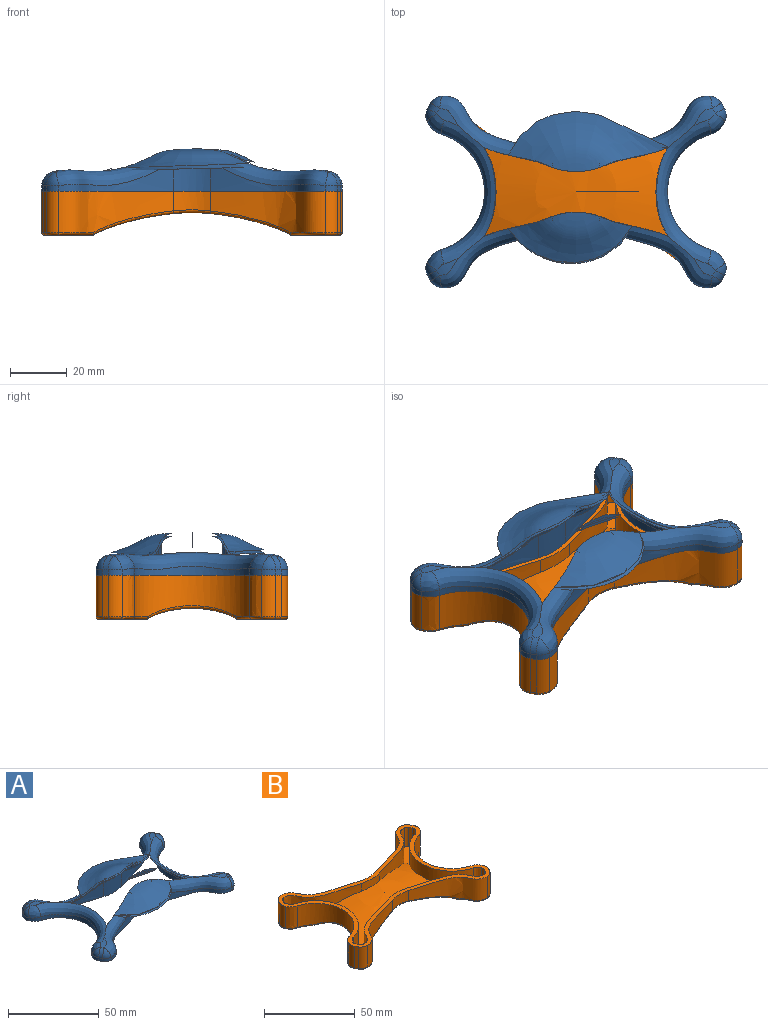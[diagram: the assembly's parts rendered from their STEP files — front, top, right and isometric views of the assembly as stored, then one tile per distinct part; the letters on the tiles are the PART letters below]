
ASSEMBLY  parts=2 mates=1
PART A: 107 faces, bbox 106.7x73.2x17.5 mm
  f0: plane 106.75x70.16mm, normal (0,0,-1), area 398.4mm2, adj f5,f6,f7,f10,f11,f13,f14,f15
  f1: revolved ~72.28x72.28mm, area 1741.4mm2, adj f35,f42,f43,f47,f48,f49,f50,f51
  f2: revolved ~9.21x7.37mm, area 20mm2, adj f12,f37,f43,f48
  f3: revolved ~9.21x7.37mm, area 20mm2, adj f20,f35,f36,f43
  f4: revolved ~9.21x7.37mm, area 20mm2, adj f8,f45,f49,f51
  f5: extruded ~4.79x4.26mm, area 14.9mm2, adj f0,f22,f32,f45
  f6: extruded ~4.79x4.26mm, area 14.9mm2, adj f0,f23,f28,f37
  f7: cylinder r=60mm len=2mm, axis (0,0,-1), area 4.4mm2, adj f0,f8,f32,f53
  f8: torus R=55mm, axis (0,0,-1), area 14.2mm2, adj f4,f7,f39,f52
  f9: revolved ~9.21x7.37mm, area 20mm2, adj f17,f46,f47,f49
  f10: extruded ~40.46x20.84mm, area 177.5mm2, adj f0,f25,f51,f53
  f11: cylinder r=60mm len=2mm, axis (0,0,-1), area 4.4mm2, adj f0,f12,f28,f38
  f12: torus R=55mm, axis (0,0,-1), area 14.2mm2, adj f2,f11,f31,f44
  f13: extruded ~40.46x20.84mm, area 177.5mm2, adj f0,f25,f38,f48
  f14: extruded ~4.79x4.26mm, area 14.9mm2, adj f0,f22,f33,f46
  f15: extruded ~4.79x4.26mm, area 14.9mm2, adj f0,f23,f27,f36
  f16: cylinder r=60mm len=2mm, axis (0,0,-1), area 4.4mm2, adj f0,f17,f33,f34
  f17: torus R=55mm, axis (0,0,-1), area 14.2mm2, adj f9,f16,f40,f41
  f18: extruded ~40.46x20.84mm, area 177.5mm2, adj f0,f24,f34,f47
  f19: cylinder r=60mm len=2mm, axis (0,0,-1), area 4.4mm2, adj f0,f20,f26,f27
  f20: torus R=55mm, axis (0,0,-1), area 14.2mm2, adj f3,f19,f29,f30
  f21: extruded ~40.46x20.84mm, area 177.5mm2, adj f0,f24,f26,f35
  f22: cylinder r=21.18mm len=40.7mm, axis (0,0,-1), area 131.2mm2, adj f0,f5,f14,f49
  f23: cylinder r=21.18mm len=40.7mm, axis (0,0,-1), area 131.2mm2, adj f0,f6,f15,f43
  f24: cylinder r=21.18mm len=12.96mm, axis (0,0,-1), area 123.5mm2, adj f0,f18,f21,f42
  f25: cylinder r=21.18mm len=12.96mm, axis (0,0,-1), area 123.5mm2, adj f0,f10,f13,f50
  f26: cylinder r=5mm len=4.22mm, axis (0,0,-1), area 10.1mm2, adj f0,f19,f21,f29
  f27: cylinder r=5mm len=4.85mm, axis (0,0,-1), area 10.1mm2, adj f0,f15,f19,f30
  f28: cylinder r=5mm len=4.85mm, axis (0,0,-1), area 10.1mm2, adj f0,f6,f11,f31
  f29: sphere r=5mm, area 22.3mm2, adj f20,f26,f35
  f30: sphere r=5mm, area 22.4mm2, adj f20,f27,f36
  f31: sphere r=5mm, area 22.4mm2, adj f12,f28,f37
  f32: cylinder r=5mm len=4.85mm, axis (0,0,-1), area 10.1mm2, adj f0,f5,f7,f39
  f33: cylinder r=5mm len=4.85mm, axis (0,0,-1), area 10.1mm2, adj f0,f14,f16,f40
  f34: cylinder r=5mm len=4.22mm, axis (0,0,-1), area 10.1mm2, adj f0,f16,f18,f41
  f35: bspline ~43.55x25.83mm, area 367.1mm2, adj f1,f3,f21,f29,f42,f43
  f36: bspline ~7.62x6.92mm, area 42.9mm2, adj f3,f15,f30,f43
  f37: bspline ~7.52x6.6mm, area 42.9mm2, adj f2,f6,f31,f43
  f38: cylinder r=5mm len=4.22mm, axis (0,0,-1), area 10.1mm2, adj f0,f11,f13,f44
  f39: sphere r=5mm, area 22.4mm2, adj f8,f32,f45
  f40: sphere r=5mm, area 22.4mm2, adj f17,f33,f46
  f41: sphere r=5mm, area 20.1mm2, adj f17,f34,f47
  f42: bspline ~18.18x6.2mm, area 114.7mm2, adj f1,f24,f35,f47
  f43: bspline ~51.29x20.77mm, area 447.9mm2, adj f1,f2,f3,f23,f35,f36,f37,f48
  f44: sphere r=5mm, area 20.1mm2, adj f12,f38,f48
  f45: bspline ~7.62x6.92mm, area 42.9mm2, adj f4,f5,f39,f49
  f46: bspline ~7.52x6.6mm, area 42.9mm2, adj f9,f14,f40,f49
  f47: bspline ~42.5x25.43mm, area 367.1mm2, adj f1,f9,f18,f41,f42,f49
  f48: bspline ~42.5x25.43mm, area 367.1mm2, adj f1,f2,f13,f43,f44,f50
  f49: bspline ~51.29x20.77mm, area 447.9mm2, adj f1,f4,f9,f22,f45,f46,f47,f51
  f50: bspline ~18.18x6.2mm, area 114.7mm2, adj f1,f25,f48,f51
  f51: bspline ~43.55x25.83mm, area 367.1mm2, adj f1,f4,f10,f49,f50,f52
  f52: sphere r=5mm, area 22.3mm2, adj f8,f51,f53
  f53: cylinder r=5mm len=4.22mm, axis (0,0,-1), area 10.1mm2, adj f0,f7,f10,f52
  f54: revolved ~72.22x72.22mm, area 1719.6mm2, adj f88,f95,f96,f100,f101,f102,f103,f104
  f55: revolved ~8.96x7.22mm, area 19.2mm2, adj f65,f90,f96,f101
  f56: revolved ~8.96x7.22mm, area 19.2mm2, adj f73,f88,f89,f96
  f57: revolved ~8.96x7.22mm, area 19.2mm2, adj f61,f98,f102,f104
  f58: extruded ~4.19x3.78mm, area 13.1mm2, adj f0,f75,f85,f98
  f59: extruded ~4.19x3.78mm, area 13.1mm2, adj f0,f76,f81,f90
  f60: cylinder r=59mm len=2mm, axis (0,0,-1), area 4.3mm2, adj f0,f61,f85,f106
  f61: torus R=55mm, axis (0,0,-1), area 11.2mm2, adj f57,f60,f92,f105
  f62: revolved ~8.96x7.22mm, area 19.2mm2, adj f70,f99,f100,f102
  f63: extruded ~40.14x20.79mm, area 176.4mm2, adj f0,f78,f104,f106
  f64: cylinder r=59mm len=2mm, axis (0,0,-1), area 4.3mm2, adj f0,f65,f81,f91
  f65: torus R=55mm, axis (0,0,-1), area 11.2mm2, adj f55,f64,f84,f97
  f66: extruded ~40.14x20.79mm, area 176.4mm2, adj f0,f78,f91,f101
  f67: extruded ~4.19x3.78mm, area 13.1mm2, adj f0,f75,f86,f99
  f68: extruded ~4.19x3.78mm, area 13.1mm2, adj f0,f76,f80,f89
  f69: cylinder r=59mm len=2mm, axis (0,0,-1), area 4.3mm2, adj f0,f70,f86,f87
  f70: torus R=55mm, axis (0,0,-1), area 11.2mm2, adj f62,f69,f93,f94
  f71: extruded ~40.14x20.79mm, area 176.4mm2, adj f0,f77,f87,f100
  f72: cylinder r=59mm len=2mm, axis (0,0,-1), area 4.3mm2, adj f0,f73,f79,f80
  f73: torus R=55mm, axis (0,0,-1), area 11.2mm2, adj f56,f72,f82,f83
  f74: extruded ~40.14x20.79mm, area 176.4mm2, adj f0,f77,f79,f88
  f75: cylinder r=22.18mm len=42.62mm, axis (0,0,-1), area 137.4mm2, adj f0,f58,f67,f102
  f76: cylinder r=22.18mm len=42.62mm, axis (0,0,-1), area 137.4mm2, adj f0,f59,f68,f96
  f77: cylinder r=22.18mm len=13.57mm, axis (0,0,-1), area 129.3mm2, adj f0,f71,f74,f95
  f78: cylinder r=22.18mm len=13.57mm, axis (0,0,-1), area 129.3mm2, adj f0,f63,f66,f103
  f79: cylinder r=4mm len=3.37mm, axis (0,0,-1), area 8.1mm2, adj f0,f72,f74,f82
  f80: cylinder r=4mm len=3.88mm, axis (0,0,-1), area 8.1mm2, adj f0,f68,f72,f83
  f81: cylinder r=4mm len=3.88mm, axis (0,0,-1), area 8.1mm2, adj f0,f59,f64,f84
  f82: sphere r=4mm, area 14.2mm2, adj f73,f79,f88
  f83: sphere r=4mm, area 14.3mm2, adj f73,f80,f89
  f84: sphere r=4mm, area 12.9mm2, adj f65,f81,f90
  f85: cylinder r=4mm len=3.88mm, axis (0,0,-1), area 8.1mm2, adj f0,f58,f60,f92
  f86: cylinder r=4mm len=3.88mm, axis (0,0,-1), area 8.1mm2, adj f0,f67,f69,f93
  f87: cylinder r=4mm len=3.37mm, axis (0,0,-1), area 8.1mm2, adj f0,f69,f71,f94
  f88: bspline ~43.02x24.9mm, area 292.3mm2, adj f54,f56,f74,f82,f95,f96
  f89: bspline ~6.19x4.98mm, area 30.7mm2, adj f56,f68,f83,f96
  f90: bspline ~6.19x4.98mm, area 30.7mm2, adj f55,f59,f84,f96
  f91: cylinder r=4mm len=3.37mm, axis (0,0,-1), area 8.1mm2, adj f0,f64,f66,f97
  f92: sphere r=4mm, area 14.3mm2, adj f61,f85,f98
  f93: sphere r=4mm, area 12.9mm2, adj f70,f86,f99
  f94: sphere r=4mm, area 14.2mm2, adj f70,f87,f100
  f95: bspline ~16.98x4.84mm, area 93.1mm2, adj f54,f77,f88,f100
  f96: bspline ~50.65x19.13mm, area 368mm2, adj f54,f55,f56,f76,f88,f89,f90,f101
  f97: sphere r=4mm, area 14.2mm2, adj f65,f91,f101
  f98: bspline ~6.19x4.98mm, area 30.7mm2, adj f57,f58,f92,f102
  f99: bspline ~6.19x4.98mm, area 30.7mm2, adj f62,f67,f93,f102
  f100: bspline ~42.05x24.52mm, area 292.3mm2, adj f54,f62,f71,f94,f95,f102
  f101: bspline ~42.05x24.52mm, area 292.3mm2, adj f54,f55,f66,f96,f97,f103
  f102: bspline ~50.65x19.13mm, area 368mm2, adj f54,f57,f62,f75,f98,f99,f100,f104
  f103: bspline ~16.98x4.84mm, area 93.1mm2, adj f54,f78,f101,f104
  f104: bspline ~43.02x24.9mm, area 292.3mm2, adj f54,f57,f63,f102,f103,f105
  f105: sphere r=4mm, area 14.2mm2, adj f61,f104,f106
  f106: cylinder r=4mm len=3.37mm, axis (0,0,-1), area 8.1mm2, adj f0,f60,f63,f105
PART B: 103 faces, bbox 119.4x84.8x17.4 mm
  f0: extruded ~40.46x20.84mm, area 548.2mm2, adj f1,f12,f28,f41,f42
  f1: cylinder r=21.18mm len=12.96mm, axis (0,0,1), area 90.8mm2, adj f0,f2,f28,f37
  f2: extruded ~40.46x20.84mm, area 548.2mm2, adj f1,f13,f28,f32,f33
  f3: cylinder r=21.18mm len=40.7mm, axis (0,0,1), area 705mm2, adj f16,f17,f28,f44,f52,f53
  f4: extruded ~40.46x20.84mm, area 548.2mm2, adj f5,f20,f28,f64,f70
  f5: cylinder r=21.18mm len=12.96mm, axis (0,0,1), area 90.8mm2, adj f4,f6,f28,f72
  f6: extruded ~40.46x20.84mm, area 548.2mm2, adj f5,f21,f28,f68,f73
  f7: cylinder r=21.18mm len=40.7mm, axis (0,0,1), area 705mm2, adj f24,f25,f28,f50,f61,f62
  f8: plane 16.64x16.49mm, normal (0,0,-1), area 155.2mm2, adj f30,f31,f33,f34,f39,f43,f44
  f9: plane 16.64x16.49mm, normal (0,0,-1), area 155.2mm2, adj f35,f36,f40,f41,f45,f50,f51
  f10: plane 16.64x16.49mm, normal (0,0,-1), area 155.2mm2, adj f55,f56,f60,f61,f65,f68,f69
  f11: cylinder r=60mm len=14.5mm, axis (0,0,1), area 32mm2, adj f12,f26,f28,f35
  f12: cylinder r=5mm len=14.5mm, axis (0,0,1), area 73.4mm2, adj f0,f11,f28,f36
  f13: cylinder r=5mm len=14.5mm, axis (0,0,1), area 73.4mm2, adj f2,f14,f28,f30
  f14: cylinder r=60mm len=14.5mm, axis (0,0,1), area 32mm2, adj f13,f15,f28,f31
  f15: cylinder r=5mm len=14.5mm, axis (0,0,1), area 73.4mm2, adj f14,f16,f28,f34
  f16: extruded ~14.5x4.79mm, area 95.6mm2, adj f3,f15,f28,f39
  f17: extruded ~14.5x4.79mm, area 95.6mm2, adj f3,f18,f28,f48
  f18: cylinder r=5mm len=14.5mm, axis (0,0,1), area 73.4mm2, adj f17,f19,f28,f49
  f19: cylinder r=60mm len=14.5mm, axis (0,0,1), area 32mm2, adj f18,f20,f28,f54
  f20: cylinder r=5mm len=14.5mm, axis (0,0,1), area 73.4mm2, adj f4,f19,f28,f59
  f21: cylinder r=5mm len=14.5mm, axis (0,0,1), area 73.4mm2, adj f6,f22,f28,f65
  f22: cylinder r=60mm len=14.5mm, axis (0,0,1), area 32mm2, adj f21,f23,f28,f60
  f23: cylinder r=5mm len=14.5mm, axis (0,0,1), area 73.4mm2, adj f22,f24,f28,f55
  f24: extruded ~14.5x4.79mm, area 95.6mm2, adj f7,f23,f28,f56
  f25: extruded ~14.5x4.79mm, area 95.6mm2, adj f7,f26,f28,f45
  f26: cylinder r=5mm len=14.5mm, axis (0,0,1), area 73.4mm2, adj f11,f25,f28,f40
  f27: plane 16.64x16.49mm, normal (0,0,-1), area 155.2mm2, adj f48,f49,f53,f54,f59,f63,f64
  f28: plane 106.85x68.65mm, normal (0,0,1), area 983.5mm2, adj f0,f1,f2,f3,f4,f5,f6,f7
  f29: sphere r=105mm, area 2088.8mm2, adj f32,f37,f42,f43,f51,f52,f62,f63
  f30: torus R=4mm, axis (0,0,1), area 7.4mm2, adj f8,f13,f31,f33
  f31: torus R=59mm, axis (0,0,1), area 3.4mm2, adj f8,f14,f30,f34
  f32: bspline ~38.56x14.8mm, area 51mm2, adj f2,f29,f37,f38
  f33: bspline ~25.9x12.77mm, area 27.1mm2, adj f2,f8,f30,f38
  f34: torus R=4mm, axis (0,0,1), area 7.4mm2, adj f8,f15,f31,f39
  f35: torus R=59mm, axis (0,0,1), area 3.4mm2, adj f9,f11,f36,f40
  f36: torus R=4mm, axis (0,0,1), area 7.4mm2, adj f9,f12,f35,f41
  f37: bspline ~18.02x2.96mm, area 22.2mm2, adj f1,f29,f32,f42
  f38: sphere r=1mm, area 0.4mm2, adj f32,f33,f43
  f39: bspline ~7.07x6.87mm, area 9.9mm2, adj f8,f16,f34,f44
  f40: torus R=4mm, axis (0,0,1), area 7.4mm2, adj f9,f26,f35,f45
  f41: bspline ~25.9x12.77mm, area 27.1mm2, adj f0,f9,f36,f46
  f42: bspline ~40.35x14.93mm, area 51mm2, adj f0,f29,f37,f46
  f43: torus R=41.6mm, axis (0,0,1), area 2.6mm2, adj f8,f29,f38,f47
  f44: torus R=22.18mm, axis (0,0,1), area 15.8mm2, adj f3,f8,f39,f47
  f45: bspline ~7.07x6.87mm, area 9.9mm2, adj f9,f25,f40,f50
  f46: sphere r=1mm, area 0.4mm2, adj f41,f42,f51
  f47: sphere r=1mm, area 0.4mm2, adj f43,f44,f52
  f48: bspline ~7.07x6.87mm, area 9.9mm2, adj f17,f27,f49,f53
  f49: torus R=4mm, axis (0,0,1), area 7.4mm2, adj f18,f27,f48,f54
  f50: torus R=22.18mm, axis (0,0,1), area 15.8mm2, adj f7,f9,f45,f57
  f51: torus R=41.6mm, axis (0,0,1), area 2.6mm2, adj f9,f29,f46,f57
  f52: bspline ~34.55x9.63mm, area 65.5mm2, adj f3,f29,f47,f58
  f53: torus R=22.18mm, axis (0,0,1), area 15.8mm2, adj f3,f27,f48,f58
  f54: torus R=59mm, axis (0,0,1), area 3.4mm2, adj f19,f27,f49,f59
  f55: torus R=4mm, axis (0,0,1), area 7.4mm2, adj f10,f23,f56,f60
  f56: bspline ~7.07x6.87mm, area 9.9mm2, adj f10,f24,f55,f61
  f57: sphere r=1mm, area 0.4mm2, adj f50,f51,f62
  f58: sphere r=1mm, area 0.4mm2, adj f52,f53,f63
  f59: torus R=4mm, axis (0,0,1), area 7.4mm2, adj f20,f27,f54,f64
  f60: torus R=59mm, axis (0,0,1), area 3.4mm2, adj f10,f22,f55,f65
  f61: torus R=22.18mm, axis (0,0,1), area 15.8mm2, adj f7,f10,f56,f66
  f62: bspline ~34.55x9.63mm, area 65.5mm2, adj f7,f29,f57,f66
  f63: torus R=41.6mm, axis (0,0,1), area 2.6mm2, adj f27,f29,f58,f67
  f64: bspline ~25.9x12.77mm, area 27.1mm2, adj f4,f27,f59,f67
  f65: torus R=4mm, axis (0,0,1), area 7.4mm2, adj f10,f21,f60,f68
  f66: sphere r=1mm, area 0.4mm2, adj f61,f62,f69
  f67: sphere r=1mm, area 0.4mm2, adj f63,f64,f70
  f68: bspline ~25.9x12.77mm, area 27.1mm2, adj f6,f10,f65,f71
  f69: torus R=41.6mm, axis (0,0,1), area 2.6mm2, adj f10,f29,f66,f71
  f70: bspline ~40.35x14.93mm, area 51mm2, adj f4,f29,f67,f72
  f71: sphere r=1mm, area 0.4mm2, adj f68,f69,f73
  f72: bspline ~18.02x2.96mm, area 22.2mm2, adj f5,f29,f70,f73
  f73: bspline ~38.56x14.8mm, area 51mm2, adj f6,f29,f71,f72
  f74: extruded ~39.67x20.72mm, area 472.9mm2, adj f28,f75,f83,f86,f102
  f75: cylinder r=23.68mm len=14.49mm, axis (0,0,1), area 77.5mm2, adj f28,f74,f76,f102
  f76: extruded ~39.67x20.72mm, area 460.4mm2, adj f28,f75,f82,f87,f102
  f77: cylinder r=23.68mm len=45.51mm, axis (0,0,1), area 678.7mm2, adj f28,f82,f90,f91,f101,f102
  f78: extruded ~39.67x20.72mm, area 460.1mm2, adj f28,f79,f94,f101,f102
  f79: cylinder r=23.68mm len=14.49mm, axis (0,0,1), area 77.5mm2, adj f28,f78,f80,f102
  f80: extruded ~39.67x20.72mm, area 460.4mm2, adj f28,f79,f84,f95,f102
  f81: cylinder r=23.68mm len=45.51mm, axis (0,0,1), area 678.7mm2, adj f28,f83,f84,f98,f99,f102
  f82: plane 15.14x14.37mm, normal (0,0,1), area 93.1mm2, adj f76,f77,f87,f88,f89,f90,f102
  f83: plane 15.14x14.37mm, normal (0,0,1), area 93mm2, adj f74,f81,f85,f86,f99,f100,f102
  f84: plane 15.14x14.37mm, normal (0,0,1), area 93mm2, adj f80,f81,f95,f96,f97,f98,f102
  f85: cylinder r=57.5mm len=13mm, axis (0,0,1), area 27.5mm2, adj f28,f83,f86,f100
  f86: cylinder r=2.5mm len=13mm, axis (0,0,1), area 32.9mm2, adj f28,f74,f83,f85
  f87: cylinder r=2.5mm len=13mm, axis (0,0,1), area 32.9mm2, adj f28,f76,f82,f88
  f88: cylinder r=57.5mm len=13mm, axis (0,0,1), area 27.5mm2, adj f28,f82,f87,f89
  f89: cylinder r=2.5mm len=13mm, axis (0,0,1), area 32.9mm2, adj f28,f82,f88,f90
  f90: extruded ~13x3.28mm, area 60mm2, adj f28,f77,f82,f89
  f91: extruded ~13x3.28mm, area 60mm2, adj f28,f77,f92,f101
  f92: cylinder r=2.5mm len=13mm, axis (0,0,1), area 32.9mm2, adj f28,f91,f93,f101
  f93: cylinder r=57.5mm len=13mm, axis (0,0,1), area 27.5mm2, adj f28,f92,f94,f101
  f94: cylinder r=2.5mm len=13mm, axis (0,0,1), area 32.9mm2, adj f28,f78,f93,f101
  f95: cylinder r=2.5mm len=13mm, axis (0,0,1), area 32.9mm2, adj f28,f80,f84,f96
  f96: cylinder r=57.5mm len=13mm, axis (0,0,1), area 27.5mm2, adj f28,f84,f95,f97
  f97: cylinder r=2.5mm len=13mm, axis (0,0,1), area 32.9mm2, adj f28,f84,f96,f98
  f98: extruded ~13x3.28mm, area 60mm2, adj f28,f81,f84,f97
  f99: extruded ~13x3.28mm, area 60mm2, adj f28,f81,f83,f100
  f100: cylinder r=2.5mm len=13mm, axis (0,0,1), area 32.9mm2, adj f28,f83,f85,f99
  f101: plane 15.14x14.37mm, normal (0,0,1), area 93.1mm2, adj f77,f78,f91,f92,f93,f94,f102
  f102: sphere r=107.5mm, area 1777.4mm2, adj f74,f75,f76,f77,f78,f79,f80,f81
PLACE A t=(-4.07,4.7,-5.59)mm
PLACE B t=(-4.07,4.7,-5.59)mm
MATE fastened A.f0 <-> B.f28  axis (0,0,1) through (48.23,29.32,-5.59)mm
